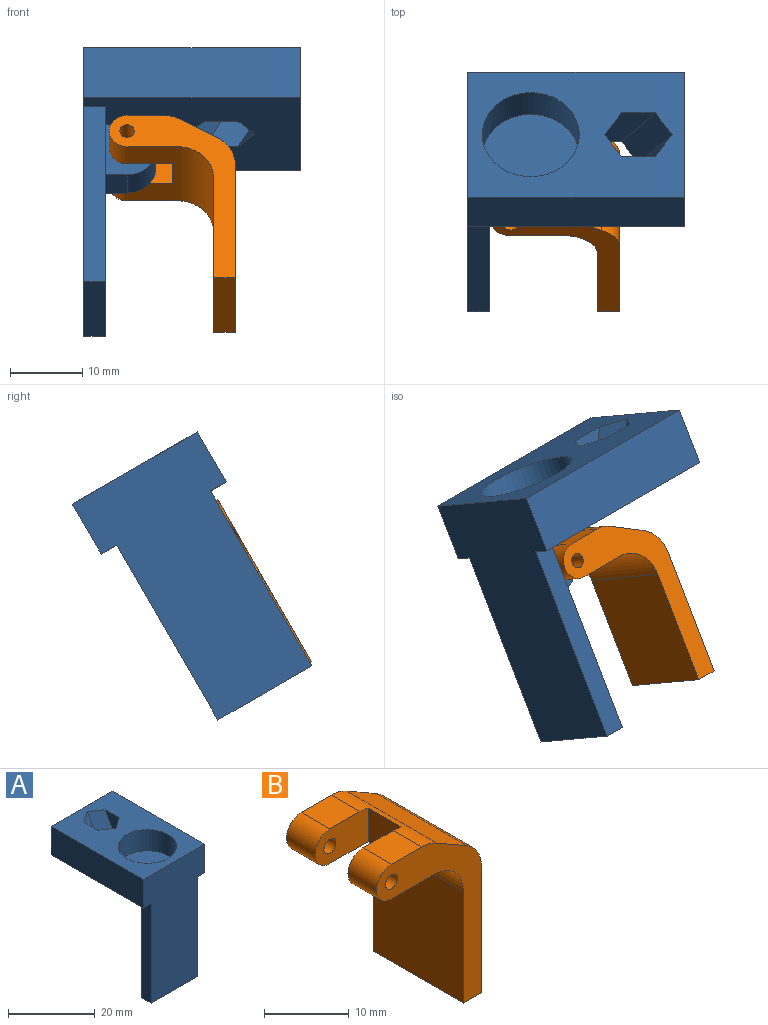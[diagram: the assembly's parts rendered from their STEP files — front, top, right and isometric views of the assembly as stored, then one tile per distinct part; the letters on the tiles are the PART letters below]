
ASSEMBLY  parts=2 mates=1
PART A: 24 faces, bbox 20x30x36 mm
  f0: plane 30x20mm, normal (0,0,-1), area 471mm2, adj f3,f4,f5,f6,f7,f8,f9,f12
  f1: plane 30x20mm, normal (0,0,1), area 408.7mm2, adj f5,f7,f8,f9,f10,f12,f13,f14
  f2: plane 15x3mm, normal (0,0,-1), area 45mm2, adj f3,f4,f5,f6
  f3: plane 28x3mm, normal (1,0,0), area 84mm2, adj f0,f2,f5,f6
  f4: plane 28x3mm, normal (-1,0,0), area 84mm2, adj f0,f2,f5,f6
  f5: plane 36x20mm, normal (0,-1,0), area 580mm2, adj f0,f1,f2,f3,f4,f7,f8
  f6: plane 28x15mm, normal (0,1,0), area 380mm2, adj f0,f2,f3,f4,f18,f22,f23
  f7: plane 30x8mm, normal (-1,0,0), area 240mm2, adj f0,f1,f5,f9
  f8: plane 30x8mm, normal (1,0,0), area 240mm2, adj f0,f1,f5,f9
  f9: plane 20x8mm, normal (0,1,0), area 160mm2, adj f0,f1,f7,f8
  f10: cylinder r=6.73mm len=13.46mm, axis (0,0,1), area 253.8mm2, adj f1,f11
  f11: plane 13.46x13.46mm, normal (0,0,1), area 142.3mm2, adj f10
  f12: plane 8x6.95mm, normal (0.5,-0.75,0.43), area 37.3mm2, adj f0,f1,f13,f17
  f13: plane 8x6.95mm, normal (-0.5,-0.75,0.43), area 37.3mm2, adj f0,f1,f12,f14
  f14: plane 9.29x8mm, normal (-1,0,0), area 37.3mm2, adj f0,f1,f13,f15
  f15: plane 8x6.95mm, normal (-0.5,0.75,-0.43), area 37.3mm2, adj f0,f1,f14,f16
  f16: plane 8x6.95mm, normal (0.5,0.75,-0.43), area 37.3mm2, adj f0,f1,f15,f17
  f17: plane 9.29x8mm, normal (1,0,0), area 37.3mm2, adj f0,f1,f12,f16
  f18: plane 5x3mm, normal (0,0,-1), area 15mm2, adj f6,f19,f22,f23
  f19: cylinder r=4mm len=5mm, axis (-1,0,0), area 31.4mm2, adj f18,f20,f22,f23
  f20: plane 5x4mm, normal (0,1,0), area 20mm2, adj f0,f19,f22,f23
  f21: cylinder r=1mm len=5mm, axis (-1,0,0), area 31.4mm2, adj f22,f23
  f22: plane 8x7mm, normal (1,0,0), area 49.4mm2, adj f0,f6,f18,f19,f20,f21
  f23: plane 8x7mm, normal (-1,0,0), area 49.4mm2, adj f0,f6,f18,f19,f20,f21
PART B: 19 faces, bbox 17.5x15x26 mm
  f0: plane 5x4.75mm, normal (0,0,1), area 23.8mm2, adj f2,f12,f14,f18
  f1: plane 15x5mm, normal (0.5,0,0.87), area 86.6mm2, adj f11,f12,f17,f18
  f2: cylinder r=2.5mm len=5mm, axis (0,1,0), area 37.3mm2, adj f0,f7,f12,f14
  f3: cylinder r=1mm len=4.75mm, axis (0,1,0), area 29.8mm2, adj f12,f14
  f4: plane 18.11x15mm, normal (1,0,0), area 271.7mm2, adj f9,f11,f12,f17
  f5: plane 5x4.75mm, normal (0,0,1), area 23.7mm2, adj f6,f11,f15,f18
  f6: cylinder r=2.5mm len=5mm, axis (0,1,0), area 37.3mm2, adj f5,f7,f11,f15
  f7: plane 15x7mm, normal (0,0,-1), area 70.1mm2, adj f2,f6,f11,f12,f13,f14,f15,f16
  f8: plane 16x15mm, normal (-1,0,0), area 240mm2, adj f9,f11,f12,f13
  f9: plane 15x3mm, normal (0,0,-1), area 45mm2, adj f4,f8,f11,f12
  f10: cylinder r=1mm len=4.75mm, axis (0,1,0), area 29.8mm2, adj f11,f15
  f11: plane 26x17.5mm, normal (0,-1,0), area 126.9mm2, adj f1,f4,f5,f6,f7,f8,f9,f10
  f12: plane 26x17.5mm, normal (0,1,0), area 126.9mm2, adj f0,f1,f2,f3,f4,f7,f8,f9
  f13: cylinder r=5mm len=15mm, axis (0,1,0), area 117.8mm2, adj f7,f8,f11,f12
  f14: plane 8.84x5mm, normal (0,-1,0), area 38.3mm2, adj f0,f2,f3,f7,f16,f18
  f15: plane 8.84x5mm, normal (0,1,0), area 38.3mm2, adj f5,f6,f7,f10,f16,f18
  f16: plane 5.5x4.82mm, normal (-1,0,0), area 26.5mm2, adj f7,f14,f15,f18
  f17: cylinder r=5mm len=15mm, axis (0,-1,0), area 78.5mm2, adj f1,f4,f11,f12
  f18: cylinder r=5mm len=15mm, axis (0,1,0), area 31.8mm2, adj f0,f1,f5,f11,f12,f14,f15,f16
PLACE A rot(axis=(-0.25,-0.25,-0.94),93.8deg) t=(-20.15,-13.51,-8.76)mm
PLACE B rot(axis=(-1,0,0),30deg) t=(-2.15,-15.23,-11.23)mm
MATE revolute A.f19 <-> B.f2  axis (0,-0.87,0.5) through (-15.65,-10.68,1.15)mm
